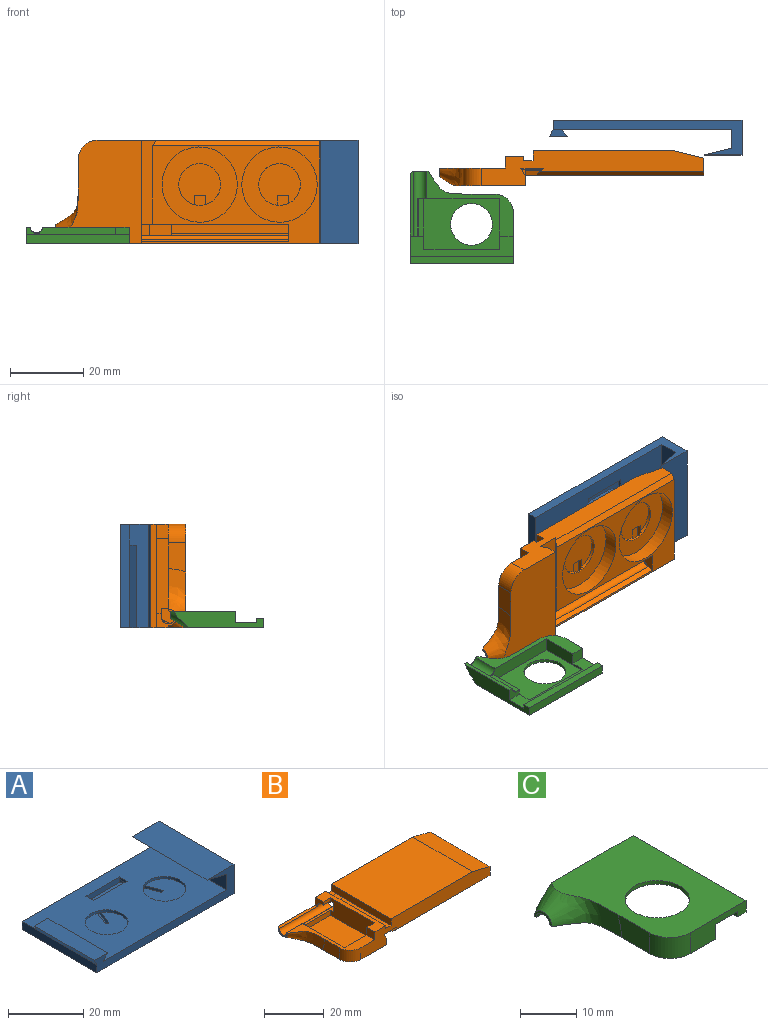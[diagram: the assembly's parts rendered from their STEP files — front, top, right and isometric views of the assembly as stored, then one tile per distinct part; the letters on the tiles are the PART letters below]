
ASSEMBLY  parts=3 mates=2
PART A: 184 faces, bbox 52.7x28.3x9.5 mm
  f0: plane 51.67x28.26mm, normal (0,0,-1), area 1320.1mm2, adj f6,f10,f11,f13,f32,f33,f34,f35
  f1: plane 2.79x0.76mm, normal (1,0,0), area 2.1mm2, adj f5,f19,f20,f22
  f2: plane 2.79x0.76mm, normal (-1,0,0), area 2.1mm2, adj f5,f19,f20,f26
  f3: cylinder r=5.71mm len=11.43mm, axis (0,0,1), area 28.5mm2, adj f4,f5,f26,f27,f28
  f4: plane 11.43x11.43mm, normal (0,0,1), area 97.2mm2, adj f3,f27,f28,f29
  f5: plane 48.9x28.26mm, normal (0,0,1), area 1089.7mm2, adj f1,f2,f3,f6,f9,f11,f13,f14
  f6: plane 51.67x9.53mm, normal (0,1,0), area 160.5mm2, adj f0,f5,f10,f12,f13,f14,f15
  f7: plane 22.54x1.88mm, normal (-0.89,0,-0.46), area 47.9mm2, adj f8,f11,f13,f16
  f8: plane 22.54x5.03mm, normal (0,0,1), area 113.3mm2, adj f7,f9,f11,f16
  f9: plane 22.54x1.88mm, normal (0.73,0,-0.68), area 58mm2, adj f5,f8,f11,f16
  f10: plane 28.26x9.53mm, normal (1,0,0), area 269.2mm2, adj f0,f6,f11,f12
  f11: plane 52.66x9.53mm, normal (0,-1,0), area 167.4mm2, adj f0,f5,f7,f8,f9,f10,f12,f13
  f12: plane 28.26x10.16mm, normal (0,0,1), area 287.1mm2, adj f6,f10,f11,f15
  f13: plane 28.26x2.6mm, normal (-1,0,0), area 73.6mm2, adj f0,f5,f6,f7,f11
  f14: plane 28.26x5.08mm, normal (-1,0,0), area 143.5mm2, adj f5,f6,f11,f15
  f15: plane 28.26x7.39mm, normal (-0.24,0,-0.97), area 215.2mm2, adj f6,f11,f12,f14
  f16: plane 5.03x1.88mm, normal (0,1,0), area 6.9mm2, adj f5,f7,f8,f9
  f17: cylinder r=5.71mm len=11.43mm, axis (0,0,1), area 28.5mm2, adj f5,f18,f22,f23,f24
  f18: plane 11.43x11.43mm, normal (0,0,1), area 97.2mm2, adj f17,f23,f24,f25
  f19: plane 12.7x1.78mm, normal (0,-1,0), area 22.6mm2, adj f1,f2,f5,f21,f24,f27
  f20: plane 12.7x1.78mm, normal (0,1,0), area 15.5mm2, adj f1,f2,f5,f21,f22,f26,f30,f31
  f21: plane 21.84x12.29mm, normal (0,0,1), area 63mm2, adj f19,f20,f23,f24,f25,f27,f28,f29
  f22: plane 7.38x6.17mm, normal (0,0,-1), area 8.4mm2, adj f1,f17,f20,f23,f24,f30
  f23: plane 6.22x2.38mm, normal (-0.93,0.36,0), area 6.6mm2, adj f17,f18,f21,f22,f25,f30
  f24: plane 11.92x4.57mm, normal (0.93,-0.36,0), area 12.8mm2, adj f17,f18,f19,f21,f22,f25
  f25: plane 0.98x0.95mm, normal (0.36,0.93,0), area 1mm2, adj f18,f21,f23,f24
  f26: plane 7.38x6.17mm, normal (0,0,-1), area 8.4mm2, adj f2,f3,f20,f27,f28,f31
  f27: plane 11.92x4.57mm, normal (-0.93,-0.36,0), area 12.8mm2, adj f3,f4,f19,f21,f26,f29
  f28: plane 6.22x2.38mm, normal (0.93,0.36,0), area 6.6mm2, adj f3,f4,f21,f26,f29,f31
  f29: plane 0.98x0.95mm, normal (-0.36,0.93,0), area 1mm2, adj f4,f21,f27,f28
  f30: cylinder r=5.08mm len=4.75mm, axis (0,0,1), area 6.2mm2, adj f20,f21,f22,f23
  f31: cylinder r=5.08mm len=4.75mm, axis (0,0,-1), area 6.2mm2, adj f20,f21,f26,f28
  f32: extruded ~0.77x0.69mm, area 0.3mm2, adj f0,f33,f36,f37
  f33: extruded ~0.77x0.7mm, area 0.3mm2, adj f0,f32,f34,f37
  f34: extruded ~0.58x0.25mm, area 0.2mm2, adj f0,f33,f35,f37
  f35: extruded ~0.51x0.25mm, area 0.1mm2, adj f0,f34,f36,f37
  f36: extruded ~0.77x0.69mm, area 0.3mm2, adj f0,f32,f35,f37
  f37: plane 1.55x1.39mm, normal (0,0,-1), area 1.8mm2, adj f32,f33,f34,f35,f36
  f38: plane 1.42x0.25mm, normal (0,1,0), area 0.4mm2, adj f0,f39,f41,f42
  f39: plane 5.2x0.25mm, normal (1,0,0), area 1.3mm2, adj f0,f38,f40,f42
  f40: plane 1.42x0.25mm, normal (0,-1,0), area 0.4mm2, adj f0,f39,f41,f42
  f41: plane 5.2x0.25mm, normal (-1,0,0), area 1.3mm2, adj f0,f38,f40,f42
  f42: plane 5.2x1.42mm, normal (0,0,-1), area 7.4mm2, adj f38,f39,f40,f41
  f43: plane 1.82x0.4mm, normal (-0.98,0.21,0), area 0.5mm2, adj f0,f44,f68,f69
  f44: plane 1.54x0.25mm, normal (0,1,0), area 0.4mm2, adj f0,f43,f45,f69
  f45: plane 5.2x1.5mm, normal (0.96,0.28,0), area 1.4mm2, adj f0,f44,f46,f69
  f46: plane 1.39x0.25mm, normal (0,-1,0), area 0.4mm2, adj f0,f45,f47,f69
  f47: plane 2.3x0.62mm, normal (-0.97,-0.26,0), area 0.6mm2, adj f0,f46,f48,f69
  f48: extruded ~0.79x0.25mm, area 0.2mm2, adj f0,f47,f49,f69
  f49: extruded ~0.92x0.25mm, area 0.2mm2, adj f0,f48,f50,f69
  f50: plane 0.25x0.03mm, normal (0,-1,0), area 0mm2, adj f0,f49,f51,f69
  f51: extruded ~0.35x0.25mm, area 0.1mm2, adj f0,f50,f52,f69
  f52: extruded ~0.44x0.25mm, area 0.1mm2, adj f0,f51,f53,f69
  f53: extruded ~0.43x0.25mm, area 0.1mm2, adj f0,f52,f54,f69
  f54: extruded ~0.3x0.25mm, area 0.1mm2, adj f0,f53,f55,f69
  f55: plane 2.49x0.61mm, normal (0.97,-0.24,0), area 0.7mm2, adj f0,f54,f56,f69
  f56: plane 1.56x0.25mm, normal (0,-1,0), area 0.4mm2, adj f0,f55,f57,f69
  f57: plane 2.49x0.64mm, normal (-0.97,-0.25,0), area 0.7mm2, adj f0,f56,f58,f69
  f58: plane 0.4x0.25mm, normal (-0.98,-0.18,0), area 0.1mm2, adj f0,f57,f59,f69
  f59: extruded ~1.12x0.25mm, area 0.3mm2, adj f0,f58,f60,f69
  f60: plane 0.25x0.03mm, normal (0,-1,0), area 0mm2, adj f0,f59,f61,f69
  f61: extruded ~1.71x0.29mm, area 0.4mm2, adj f0,f60,f62,f69
  f62: plane 2.3x0.6mm, normal (0.97,-0.25,0), area 0.6mm2, adj f0,f61,f63,f69
  f63: plane 1.41x0.25mm, normal (0,-1,0), area 0.4mm2, adj f0,f62,f64,f69
  f64: plane 5.2x1.48mm, normal (-0.96,0.27,0), area 1.4mm2, adj f0,f63,f65,f69
  f65: plane 1.53x0.25mm, normal (0,1,0), area 0.4mm2, adj f0,f64,f66,f69
  f66: plane 4.12x0.95mm, normal (0.97,0.22,0), area 1.1mm2, adj f0,f65,f67,f69
  f67: plane 0.25x0.03mm, normal (0,1,0), area 0mm2, adj f0,f66,f68,f69
  f68: plane 2.3x0.54mm, normal (-0.97,0.23,0), area 0.6mm2, adj f0,f43,f67,f69
  f69: plane 7.97x5.2mm, normal (0,0,-1), area 23.1mm2, adj f43,f44,f45,f46,f47,f48,f49,f50
  f70: plane 0.55x0.25mm, normal (0.04,1,0), area 0.1mm2, adj f71,f94,f95,f183
  f71: plane 0.43x0.25mm, normal (-1,0,0), area 0.1mm2, adj f70,f72,f95,f183
  f72: extruded ~0.75x0.3mm, area 0.2mm2, adj f71,f73,f95,f183
  f73: extruded ~0.79x0.28mm, area 0.2mm2, adj f72,f74,f95,f183
  f74: extruded ~0.69x0.6mm, area 0.3mm2, adj f73,f75,f95,f183
  f75: extruded ~0.62x0.3mm, area 0.2mm2, adj f74,f94,f95,f183
  f76: plane 0.71x0.28mm, normal (-0.93,0.36,0), area 0.2mm2, adj f0,f77,f93,f95
  f77: plane 0.99x0.25mm, normal (0,1,0), area 0.3mm2, adj f0,f76,f78,f95
  f78: plane 3.46x0.25mm, normal (1,0,0), area 0.9mm2, adj f0,f77,f79,f95
  f79: extruded ~1.39x0.56mm, area 0.4mm2, adj f0,f78,f80,f95
  f80: extruded ~1.6x0.46mm, area 0.4mm2, adj f0,f79,f81,f95
  f81: extruded ~1.99x0.47mm, area 0.5mm2, adj f0,f80,f82,f95
  f82: plane 0.96x0.47mm, normal (-0.9,0.44,0), area 0.3mm2, adj f0,f81,f83,f95
  f83: extruded ~1.47x0.38mm, area 0.4mm2, adj f0,f82,f84,f95
  f84: extruded ~0.81x0.79mm, area 0.3mm2, adj f0,f83,f85,f95
  f85: plane 0.25x0.23mm, normal (-1,0,0), area 0.1mm2, adj f0,f84,f86,f95
  f86: plane 0.9x0.25mm, normal (-0.03,-1,0), area 0.2mm2, adj f0,f85,f87,f95
  f87: extruded ~1.75x0.43mm, area 0.5mm2, adj f0,f86,f88,f95
  f88: extruded ~1.22x0.58mm, area 0.4mm2, adj f0,f87,f89,f95
  f89: extruded ~1.22x0.43mm, area 0.3mm2, adj f0,f88,f90,f95
  f90: extruded ~1.18x0.43mm, area 0.3mm2, adj f0,f89,f91,f95
  f91: extruded ~0.99x0.25mm, area 0.3mm2, adj f0,f90,f92,f95
  f92: extruded ~0.74x0.63mm, area 0.2mm2, adj f0,f91,f93,f95
  f93: plane 0.25x0.04mm, normal (0,1,0), area 0mm2, adj f0,f76,f92,f95
  f94: extruded ~0.92x0.25mm, area 0.2mm2, adj f70,f75,f95,f183
  f95: plane 5.4x4.64mm, normal (0,0,-1), area 16.6mm2, adj f70,f71,f72,f73,f74,f75,f76,f77
  f96: plane 1.46x0.25mm, normal (0,-1,0), area 0.4mm2, adj f0,f97,f105,f106
  f97: plane 4.05x1.29mm, normal (-0.95,-0.3,0), area 1.1mm2, adj f0,f96,f98,f106
  f98: extruded ~1.5x0.35mm, area 0.4mm2, adj f0,f97,f99,f106
  f99: extruded ~0.66x0.25mm, area 0.2mm2, adj f0,f98,f100,f106
  f100: extruded ~0.84x0.25mm, area 0.2mm2, adj f0,f99,f101,f106
  f101: plane 4.05x1.28mm, normal (0.95,-0.3,0), area 1.1mm2, adj f0,f100,f102,f106
  f102: plane 1.46x0.25mm, normal (0,-1,0), area 0.4mm2, adj f0,f101,f103,f106
  f103: plane 6.8x2.31mm, normal (-0.95,0.32,0), area 1.8mm2, adj f0,f102,f104,f106
  f104: plane 1.57x0.25mm, normal (0,1,0), area 0.4mm2, adj f0,f103,f105,f106
  f105: plane 6.8x2.31mm, normal (0.95,0.32,0), area 1.8mm2, adj f0,f96,f104,f106
  f106: plane 6.8x6.19mm, normal (0,0,-1), area 17.8mm2, adj f96,f97,f98,f99,f100,f101,f102,f103
  f107: extruded ~0.48x0.25mm, area 0.1mm2, adj f0,f108,f119,f120
  f108: extruded ~0.9x0.27mm, area 0.2mm2, adj f0,f107,f109,f120
  f109: extruded ~0.7x0.65mm, area 0.2mm2, adj f0,f108,f110,f120
  f110: plane 0.25x0.07mm, normal (0,-1,0), area 0mm2, adj f0,f109,f111,f120
  f111: plane 0.88x0.25mm, normal (0.97,-0.23,0), area 0.2mm2, adj f0,f110,f112,f120
  f112: plane 1.07x0.25mm, normal (0,-1,0), area 0.3mm2, adj f0,f111,f113,f120
  f113: plane 5.2x0.25mm, normal (-1,0,0), area 1.3mm2, adj f0,f112,f114,f120
  f114: plane 1.42x0.25mm, normal (0,1,0), area 0.4mm2, adj f0,f113,f115,f120
  f115: plane 2.65x0.25mm, normal (1,0,0), area 0.7mm2, adj f0,f114,f116,f120
  f116: extruded ~0.98x0.38mm, area 0.3mm2, adj f0,f115,f117,f120
  f117: extruded ~1.06x0.35mm, area 0.3mm2, adj f0,f116,f118,f120
  f118: extruded ~0.42x0.25mm, area 0.1mm2, adj f0,f117,f119,f120
  f119: plane 1.33x0.25mm, normal (1,0.08,0), area 0.3mm2, adj f0,f107,f118,f120
  f120: plane 5.3x3.38mm, normal (0,0,-1), area 9.7mm2, adj f107,f108,f109,f110,f111,f112,f113,f114
  f121: extruded ~0.89x0.25mm, area 0.2mm2, adj f0,f122,f138,f139
  f122: extruded ~0.45x0.25mm, area 0.1mm2, adj f0,f121,f123,f139
  f123: extruded ~0.45x0.25mm, area 0.1mm2, adj f0,f122,f124,f139
  f124: plane 2.51x0.25mm, normal (1,0,0), area 0.6mm2, adj f0,f123,f125,f139
  f125: plane 1.46x0.25mm, normal (0,1,0), area 0.4mm2, adj f0,f124,f126,f139
  f126: plane 1.07x0.25mm, normal (1,0,0), area 0.3mm2, adj f0,f125,f127,f139
  f127: plane 1.46x0.25mm, normal (0,-1,0), area 0.4mm2, adj f0,f126,f128,f139
  f128: plane 1.11x0.25mm, normal (1,0,0), area 0.3mm2, adj f0,f127,f129,f139
  f129: plane 0.91x0.25mm, normal (0,-1,0), area 0.2mm2, adj f0,f128,f130,f139
  f130: plane 1.1x0.41mm, normal (-0.94,-0.35,0), area 0.3mm2, adj f0,f129,f131,f139
  f131: plane 0.78x0.47mm, normal (-0.52,-0.85,0), area 0.2mm2, adj f0,f130,f132,f139
  f132: plane 0.6x0.25mm, normal (-1,0,0), area 0.2mm2, adj f0,f131,f133,f139
  f133: plane 0.68x0.25mm, normal (0,1,0), area 0.2mm2, adj f0,f132,f134,f139
  f134: plane 2.51x0.25mm, normal (-1,0,0), area 0.6mm2, adj f0,f133,f135,f139
  f135: extruded ~1.29x0.39mm, area 0.4mm2, adj f0,f134,f136,f139
  f136: extruded ~1.24x0.43mm, area 0.3mm2, adj f0,f135,f137,f139
  f137: extruded ~1.3x0.25mm, area 0.3mm2, adj f0,f136,f138,f139
  f138: plane 1.06x0.25mm, normal (1,0,0), area 0.3mm2, adj f0,f121,f137,f139
  f139: plane 6.4x3.61mm, normal (0,0,-1), area 12.1mm2, adj f121,f122,f123,f124,f125,f126,f127,f128
  f140: plane 1.42x0.25mm, normal (0,1,0), area 0.4mm2, adj f0,f141,f143,f144
  f141: plane 7.24x0.25mm, normal (1,0,0), area 1.8mm2, adj f0,f140,f142,f144
  f142: plane 1.42x0.25mm, normal (0,-1,0), area 0.4mm2, adj f0,f141,f143,f144
  f143: plane 7.24x0.25mm, normal (-1,0,0), area 1.8mm2, adj f0,f140,f142,f144
  f144: plane 7.24x1.42mm, normal (0,0,-1), area 10.3mm2, adj f140,f141,f142,f143
  f145: extruded ~1.96x0.69mm, area 0.5mm2, adj f0,f146,f164,f165
  f146: extruded ~1.03x0.25mm, area 0.3mm2, adj f0,f145,f147,f165
  f147: extruded ~0.79x0.28mm, area 0.2mm2, adj f0,f146,f148,f165
  f148: plane 1.1x0.25mm, normal (1,0,0), area 0.3mm2, adj f0,f147,f149,f165
  f149: extruded ~0.87x0.31mm, area 0.2mm2, adj f0,f148,f150,f165
  f150: extruded ~0.89x0.25mm, area 0.2mm2, adj f0,f149,f151,f165
  f151: extruded ~0.94x0.34mm, area 0.3mm2, adj f0,f150,f152,f165
  f152: extruded ~0.94x0.36mm, area 0.3mm2, adj f0,f151,f153,f165
  f153: plane 3.35x0.25mm, normal (0,1,0), area 0.9mm2, adj f0,f152,f154,f165
  f154: plane 0.69x0.25mm, normal (1,0,0), area 0.2mm2, adj f0,f153,f155,f165
  f155: extruded ~1.73x0.61mm, area 0.5mm2, adj f0,f154,f156,f165
  f156: extruded ~1.72x0.63mm, area 0.5mm2, adj f0,f155,f157,f165
  f157: extruded ~1.81x0.71mm, area 0.5mm2, adj f0,f156,f158,f165
  f158: extruded ~2.02x0.65mm, area 0.6mm2, adj f0,f157,f164,f165
  f159: extruded ~0.71x0.29mm, area 0.2mm2, adj f160,f163,f165,f166
  f160: extruded ~0.72x0.29mm, area 0.2mm2, adj f159,f161,f165,f166
  f161: extruded ~0.81x0.28mm, area 0.2mm2, adj f160,f162,f165,f166
  f162: plane 1.99x0.25mm, normal (0,-1,0), area 0.5mm2, adj f161,f163,f165,f166
  f163: extruded ~0.81x0.29mm, area 0.2mm2, adj f159,f162,f165,f166
  f164: extruded ~1.96x0.71mm, area 0.5mm2, adj f0,f145,f158,f165
  f165: plane 5.39x4.79mm, normal (0,0,-1), area 16.3mm2, adj f145,f146,f147,f148,f149,f150,f151,f152
  f166: plane 1.99x1.1mm, normal (0,0,-1), area 1.8mm2, adj f159,f160,f161,f162,f163
  f167: plane 4.4x0.25mm, normal (1,0,0), area 1.1mm2, adj f0,f168,f181,f182
  f168: plane 1.44x0.25mm, normal (0,-1,0), area 0.4mm2, adj f0,f167,f169,f182
  f169: plane 4.15x0.25mm, normal (-1,0,0), area 1.1mm2, adj f0,f168,f170,f182
  f170: extruded ~1.16x0.32mm, area 0.3mm2, adj f0,f169,f171,f182
  f171: extruded ~1.03x0.37mm, area 0.3mm2, adj f0,f170,f172,f182
  f172: extruded ~1.05x0.37mm, area 0.3mm2, adj f0,f171,f173,f182
  f173: extruded ~1.15x0.32mm, area 0.3mm2, adj f0,f172,f174,f182
  f174: plane 4.16x0.25mm, normal (1,0,0), area 1.1mm2, adj f0,f173,f175,f182
  f175: plane 1.44x0.25mm, normal (0,-1,0), area 0.4mm2, adj f0,f174,f176,f182
  f176: plane 4.38x0.25mm, normal (-1,0,0), area 1.1mm2, adj f0,f175,f177,f182
  f177: extruded ~1.84x0.73mm, area 0.5mm2, adj f0,f176,f178,f182
  f178: extruded ~2.04x0.67mm, area 0.6mm2, adj f0,f177,f179,f182
  f179: extruded ~1.51x0.3mm, area 0.4mm2, adj f0,f178,f180,f182
  f180: extruded ~0.98x0.87mm, area 0.3mm2, adj f0,f179,f181,f182
  f181: extruded ~1.32x0.34mm, area 0.4mm2, adj f0,f167,f180,f182
  f182: plane 6.89x5.58mm, normal (0,0,-1), area 21.2mm2, adj f167,f168,f169,f170,f171,f172,f173,f174
  f183: plane 1.77x1.47mm, normal (0,0,-1), area 2.1mm2, adj f70,f71,f72,f73,f74,f75,f94
PART B: 64 faces, bbox 72.5x38.9x18.2 mm
  f0: plane 15.73x0.13mm, normal (0,-1,0), area 2mm2, adj f3,f26,f30,f51
  f1: plane 32.18x0.25mm, normal (0,-1,0), area 8.2mm2, adj f27,f33,f34,f55
  f2: plane 5.52x1.76mm, normal (0,-1,0), area 2.1mm2, adj f3,f4,f18,f51,f55
  f3: plane 27.17x2.16mm, normal (0.89,0,0.46), area 58mm2, adj f0,f2,f5,f10,f12,f18,f26,f51
  f4: plane 0.28x0.26mm, normal (-0.73,0,0.68), area 0mm2, adj f2,f51,f55
  f5: plane 42.29x5.33mm, normal (0,1,0), area 191.3mm2, adj f3,f8,f10,f11,f19,f26,f27,f28
  f6: cylinder r=5.71mm len=11.43mm, axis (0,0,-1), area 30.4mm2, adj f7,f25,f43,f44,f45
  f7: plane 11.43x11.22mm, normal (0,0,-1), area 94.5mm2, adj f6,f44,f45,f47
  f8: plane 13.67x3.11mm, normal (0,0,-1), area 37mm2, adj f5,f9,f28,f33,f55,f61
  f9: plane 3.56x1.27mm, normal (0,-1,0), area 4.5mm2, adj f8,f28,f59,f61
  f10: plane 22.89x6.1mm, normal (0,0,-1), area 139.5mm2, adj f3,f5,f11,f12
  f11: plane 22.89x1.91mm, normal (-0.73,0,0.68), area 58.6mm2, adj f5,f10,f12,f19,f50
  f12: plane 60.96x9.53mm, normal (0,-1,0), area 331mm2, adj f3,f10,f11,f15,f16,f17,f18,f20
  f13: plane 71.48x9.53mm, normal (0,1,0), area 428.2mm2, adj f15,f16,f18,f19,f20,f21,f53,f56
  f14: plane 7.97x4.86mm, normal (-1,0,0), area 35mm2, adj f16,f17,f53,f63
  f15: plane 38.47x28.26mm, normal (0,0,1), area 1087mm2, adj f12,f13,f21,f58
  f16: plane 28.26x19.62mm, normal (0,0,-1), area 493.4mm2, adj f12,f13,f14,f17,f18,f53
  f17: cylinder r=5.08mm len=5.08mm, axis (0,0,-1), area 38mm2, adj f12,f14,f16,f63
  f18: plane 28.26x4.09mm, normal (1,0,0), area 74.2mm2, adj f2,f3,f12,f13,f16,f19,f55
  f19: plane 48.9x26.73mm, normal (0,0,-1), area 379.5mm2, adj f5,f11,f13,f18,f20,f22,f24,f27
  f20: plane 28.26x4.61mm, normal (1,0,0), area 129.4mm2, adj f12,f13,f19,f21,f50
  f21: plane 28.26x8.27mm, normal (0.24,0,0.97), area 240.8mm2, adj f12,f13,f15,f20
  f22: cylinder r=10.29mm len=20.57mm, axis (0,0,1), area 246.3mm2, adj f19,f23
  f23: plane 20.57x20.57mm, normal (0,0,-1), area 229.8mm2, adj f22,f35
  f24: cylinder r=10.29mm len=20.57mm, axis (0,0,1), area 246.3mm2, adj f19,f25
  f25: plane 20.57x20.57mm, normal (0,0,-1), area 229.8mm2, adj f6,f24
  f26: plane 15.73x2.54mm, normal (0,0,1), area 18.2mm2, adj f0,f3,f5,f28,f29,f30
  f27: plane 12.65x5.61mm, normal (-1,0,0), area 29.3mm2, adj f1,f5,f19,f34,f35,f36,f37,f38
  f28: plane 20.64x7.14mm, normal (-1,0,0), area 141.5mm2, adj f5,f8,f9,f26,f29,f31,f32,f59
  f29: plane 13.97x2.06mm, normal (0,-1,0), area 28.8mm2, adj f26,f28,f30,f32
  f30: plane 21.62x3.97mm, normal (1,0,0), area 81.3mm2, adj f0,f26,f29,f31,f32,f51,f63
  f31: plane 13.97x7.14mm, normal (0,1,0), area 66.7mm2, adj f28,f30,f32,f59,f62,f63
  f32: plane 20.64x13.97mm, normal (0,0,1), area 288.3mm2, adj f28,f29,f30,f31
  f33: plane 3.11x1.52mm, normal (1,0,0), area 4.2mm2, adj f1,f5,f8,f34,f55
  f34: plane 32.18x2.54mm, normal (0,0,-1), area 81.7mm2, adj f1,f5,f27,f33,f37,f42
  f35: cylinder r=5.71mm len=11.43mm, axis (0,0,-1), area 30.4mm2, adj f23,f27,f36,f38,f39
  f36: plane 11.43x11.41mm, normal (0,0,-1), area 94.7mm2, adj f27,f35,f39,f41
  f37: plane 3.05x0.28mm, normal (0,-1,0), area 0.9mm2, adj f27,f34,f39,f40
  f38: plane 5.17x3.05mm, normal (0,0,1), area 14.4mm2, adj f27,f35,f39,f48
  f39: plane 7.82x1.91mm, normal (1,0,0), area 9.7mm2, adj f5,f35,f36,f37,f38,f40,f41,f48
  f40: plane 7.82x3.05mm, normal (0,0,-1), area 23.8mm2, adj f27,f37,f39,f41
  f41: plane 3.05x0.91mm, normal (0,1,0), area 2.8mm2, adj f27,f36,f39,f40
  f42: plane 3.05x0.28mm, normal (0,-1,0), area 0.9mm2, adj f34,f44,f45,f46
  f43: plane 4.78x3.05mm, normal (0,0,1), area 14.1mm2, adj f6,f44,f45,f49
  f44: plane 7.82x1.91mm, normal (1,0,0), area 9.8mm2, adj f5,f6,f7,f42,f43,f46,f47,f49
  f45: plane 7.82x1.91mm, normal (-1,0,0), area 9.8mm2, adj f5,f6,f7,f42,f43,f46,f47,f49
  f46: plane 7.82x3.05mm, normal (0,0,-1), area 23.8mm2, adj f42,f44,f45,f47
  f47: plane 3.05x0.91mm, normal (0,1,0), area 2.8mm2, adj f7,f44,f45,f46
  f48: cylinder r=0.51mm len=3.05mm, axis (1,0,0), area 2.4mm2, adj f5,f27,f38,f39
  f49: cylinder r=0.51mm len=3.05mm, axis (1,0,0), area 2.4mm2, adj f5,f43,f44,f45
  f50: plane 45.72x1.52mm, normal (0,-0.55,-0.83), area 82.9mm2, adj f11,f12,f19,f20
  f51: cylinder r=1.78mm len=63.86mm, axis (1,0,0), area 203.8mm2, adj f0,f2,f3,f4,f30,f52,f54,f55
  f52: plane 4.57x2.31mm, normal (-1,0,0), area 3.2mm2, adj f51,f53,f60,f63
  f53: bspline ~26.75x17.6mm, area 91.7mm2, adj f13,f14,f16,f52,f60,f63
  f54: plane 2.21x1.09mm, normal (-1,0,0), area 0.8mm2, adj f51,f55
  f55: plane 45.85x5.08mm, normal (0,-0.91,-0.41), area 117mm2, adj f1,f2,f4,f8,f18,f19,f27,f33
  f56: plane 28.26x1.14mm, normal (1,0,0), area 32.3mm2, adj f12,f13,f57,f59
  f57: plane 28.26x2.54mm, normal (0,0,1), area 71.8mm2, adj f12,f13,f56,f58
  f58: plane 28.26x2.73mm, normal (-1,0,0), area 77.2mm2, adj f12,f13,f15,f57
  f59: plane 28.26x5.08mm, normal (0,0,1), area 70.2mm2, adj f9,f12,f13,f28,f31,f56,f61,f62
  f60: plane 18.1x1.11mm, normal (0,0,1), area 18.6mm2, adj f13,f51,f52,f53,f61
  f61: plane 3.81x3.18mm, normal (-1,0,0), area 7.6mm2, adj f8,f9,f13,f51,f55,f59,f60
  f62: plane 3.81x3.18mm, normal (-1,0,0), area 12.1mm2, adj f12,f31,f59,f63
  f63: plane 23.65x18.03mm, normal (0,0,1), area 81.6mm2, adj f12,f14,f17,f30,f31,f51,f52,f53
PART C: 24 faces, bbox 25.5x38.7x13.3 mm
  f0: plane 20.64x13.97mm, normal (0,0,-1), area 185.7mm2, adj f2,f7,f8,f13,f23
  f1: cylinder r=5.08mm len=5.08mm, axis (0,0,-1), area 36mm2, adj f9,f10,f12,f16
  f2: plane 13.97x3.71mm, normal (0,1,0), area 39.8mm2, adj f0,f7,f8,f16,f17,f20
  f3: bspline ~26.51x13.24mm, area 87.9mm2, adj f4,f9,f10,f11,f16,f19
  f4: plane 4.58x2.05mm, normal (-1,0,0), area 3mm2, adj f3,f6,f16,f19
  f5: plane 10.16x0.27mm, normal (0,-0.91,-0.41), area 3mm2, adj f6,f7,f14,f18
  f6: cylinder r=1.78mm len=17.78mm, axis (1,0,0), area 57.2mm2, adj f4,f5,f7,f16,f18,f19
  f7: plane 22.31x3.71mm, normal (1,0,0), area 76.4mm2, adj f0,f2,f5,f6,f13,f14,f16
  f8: plane 20.64x0.54mm, normal (-1,0,0), area 11.1mm2, adj f0,f2,f13,f20
  f9: plane 28.26x21.54mm, normal (0,0,1), area 444.9mm2, adj f1,f3,f10,f11,f12,f15,f23
  f10: plane 7.96x4.6mm, normal (-1,0,0), area 33.2mm2, adj f1,f3,f9,f16
  f11: plane 24.49x4.57mm, normal (0,1,0), area 80.6mm2, adj f3,f9,f15,f18,f19,f20,f21,f22
  f12: plane 13.97x4.51mm, normal (0,-1,0), area 41.1mm2, adj f1,f9,f15,f16,f17,f20,f21,f22
  f13: plane 13.97x2.06mm, normal (0,-1,0), area 23mm2, adj f0,f7,f8,f14,f18,f20
  f14: plane 10.16x1.56mm, normal (0,0,-1), area 15.8mm2, adj f5,f7,f13,f18
  f15: plane 28.26x2.48mm, normal (1,0,0), area 70mm2, adj f9,f11,f12,f22
  f16: plane 23.67x17.78mm, normal (0,0,-1), area 80.7mm2, adj f1,f2,f3,f4,f6,f7,f10,f12
  f17: plane 3.81x3.18mm, normal (1,0,0), area 12.1mm2, adj f2,f12,f16,f20
  f18: plane 3.81x3.18mm, normal (1,0,0), area 8.3mm2, adj f5,f6,f11,f13,f14,f19,f20
  f19: plane 17.85x1.13mm, normal (0,0,-1), area 18.7mm2, adj f3,f4,f6,f11,f18
  f20: plane 28.26x5.59mm, normal (0,0,-1), area 79.3mm2, adj f2,f8,f11,f12,f13,f17,f18,f21
  f21: plane 28.26x1.14mm, normal (-1,0,0), area 32.3mm2, adj f11,f12,f20,f22
  f22: plane 28.26x2.03mm, normal (0,0,-1), area 57.4mm2, adj f11,f12,f15,f21
  f23: cylinder r=5.71mm len=11.43mm, axis (0,0,1), area 28.5mm2, adj f0,f9
PLACE A rot(axis=(1,0,0),90deg) t=(-40.74,1.15,99.08)mm
PLACE B rot(axis=(-1,0,0),90deg) t=(-48.1,-7.2,103.14)mm
PLACE C rot(axis=(0.71,-0.71,0),180deg) t=(-79.42,-47.46,91.74)mm
MATE planar C.f9 <-> A.f11  axis (0,0,-1) through (-88.19,-13.62,86.98)mm
MATE planar C.f9 <-> B.f13  axis (0,0,-1) through (-82.58,-23.89,86.98)mm
